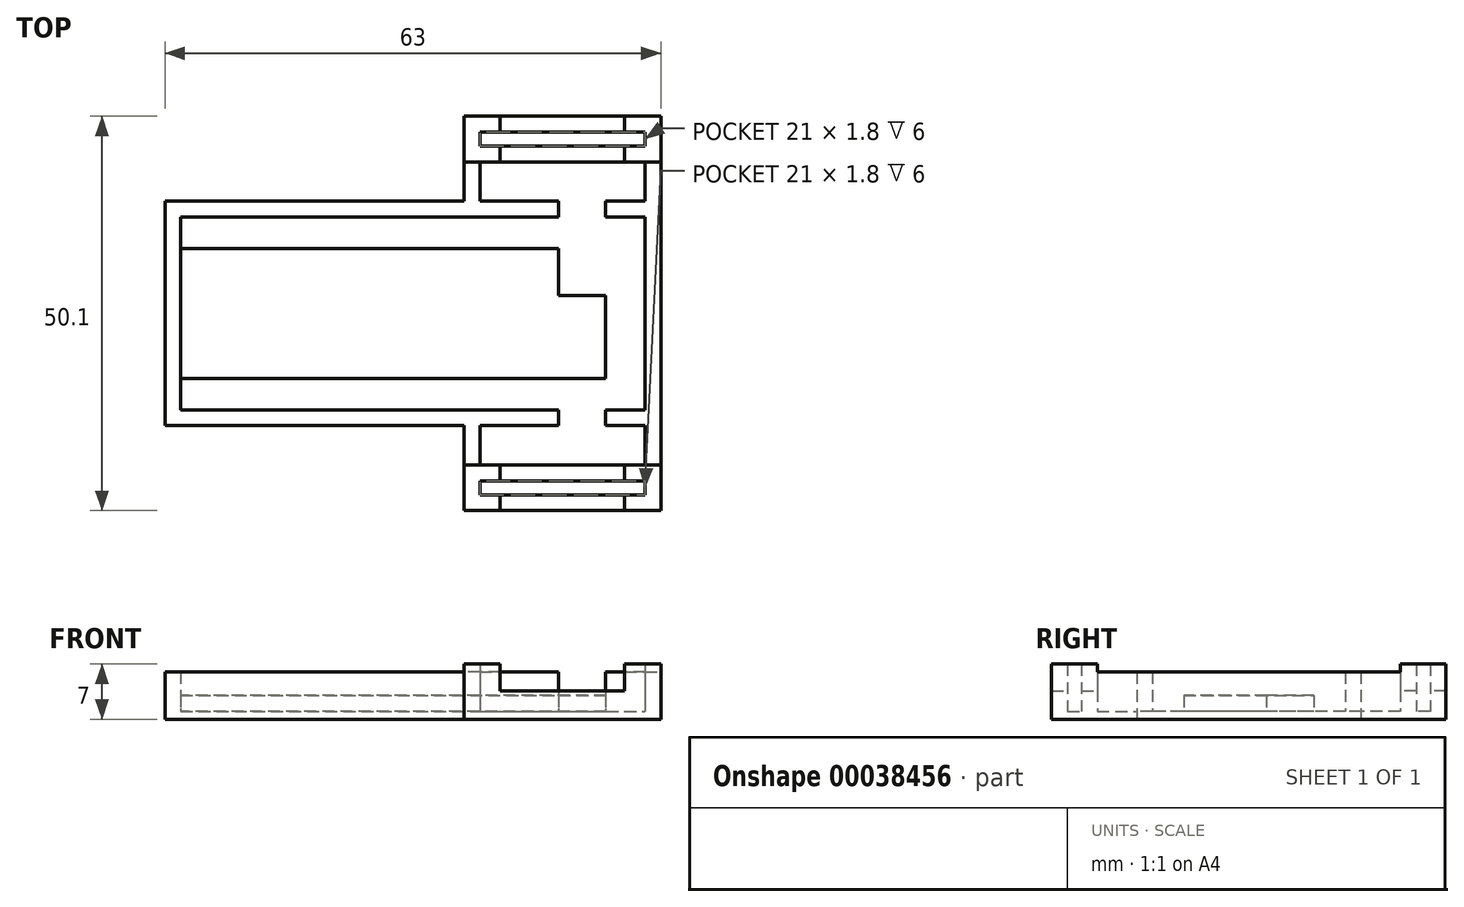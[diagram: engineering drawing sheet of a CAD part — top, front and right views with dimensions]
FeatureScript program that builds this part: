
annotation { "Feature Type Name" : "Feature", "Feature Type Description" : "" }
export const myFeature = defineFeature(function(context is Context, id is Id, definition is map)
    precondition{}
    {
        {
            var Q0;
            Q0=qCreatedBy(makeId("Top.planeOp"),FACE);
            var sketch = newSketch(context, id + "F0", { "sketchPlane" : qUnion([Q0])});
            skLineSegment(sketch, "E0", {"start": v(-83.28, 24.5) * mm, "end": v(93.04, 24.5) * mm, "construction": true});
            skLineSegment(sketch, "E1", {"start": v(59, -21.37) * mm, "end": v(59, 62.02) * mm, "construction": true});
            skLineSegment(sketch, "E2", {"start": v(-81.19, 17.1) * mm, "end": v(89.78, 17.1) * mm, "construction": true});
            skLineSegment(sketch, "E3", {"start": v(-82.58, 7.1) * mm, "end": v(88.16, 7.1) * mm, "construction": true});
            skLineSegment(sketch, "E4", {"start": v(-82.03, 20.5) * mm, "end": v(90.12, 20.5) * mm, "construction": true});
            skLineSegment(sketch, "E5", {"start": v(-82.58, 4) * mm, "end": v(90.12, 4) * mm, "construction": true});
            skLineSegment(sketch, "E6", {"start": v(54, 44.35) * mm, "end": v(54, -19.21) * mm, "construction": true});
            skLineSegment(sketch, "E7", {"start": v(-81.7, 14.5) * mm, "end": v(85.71, 14.5) * mm, "construction": true});
            skLineSegment(sketch, "E8", {"start": v(48, 44.43) * mm, "end": v(48, -19.52) * mm, "construction": true});
            skLineSegment(sketch, "E9", {"start": v(0, 20.5) * mm, "end": v(48, 20.5) * mm});
            skLineSegment(sketch, "E10", {"start": v(48, 20.5) * mm, "end": v(48, 14.5) * mm});
            skLineSegment(sketch, "E11", {"start": v(48, 14.5) * mm, "end": v(54, 14.5) * mm});
            skLineSegment(sketch, "E12", {"start": v(54, 14.5) * mm, "end": v(54, 4) * mm});
            skLineSegment(sketch, "E13", {"start": v(54, 4) * mm, "end": v(0, 4) * mm});
            skLineSegment(sketch, "E14", {"start": v(0, 4) * mm, "end": v(0, 20.5) * mm});
            skLineSegment(sketch, "E15.bottom", {"start": v(0, 24.5) * mm, "end": v(59, 24.5) * mm, "construction": true});
            skLineSegment(sketch, "E15.top", {"start": v(0, 0) * mm, "end": v(59, 0) * mm, "construction": true});
            skLineSegment(sketch, "E15.left", {"start": v(0, 24.5) * mm, "end": v(0, 0) * mm});
            skLineSegment(sketch, "E15.right", {"start": v(59, 24.5) * mm, "end": v(59, 0) * mm});
            skLineSegment(sketch, "E16.bottom", {"start": v(-2, 26.5) * mm, "end": v(61, 26.5) * mm, "construction": true});
            skLineSegment(sketch, "E16.top", {"start": v(-2, -2) * mm, "end": v(61, -2) * mm, "construction": true});
            skLineSegment(sketch, "E16.left", {"start": v(-2, 26.5) * mm, "end": v(-2, -2) * mm});
            skLineSegment(sketch, "E16.right", {"start": v(61, 26.5) * mm, "end": v(61, -2) * mm});
            skLineSegment(sketch, "E17", {"start": v(38, 55.46) * mm, "end": v(38, -21.13) * mm, "construction": true});
            skLineSegment(sketch, "E18", {"start": v(32.75, 31.5) * mm, "end": v(73.4, 31.5) * mm, "construction": true});
            skLineSegment(sketch, "E19", {"start": v(32.75, 33.5) * mm, "end": v(72.94, 33.5) * mm, "construction": true});
            skLineSegment(sketch, "E20", {"start": v(32.75, 35.3) * mm, "end": v(72.94, 35.3) * mm, "construction": true});
            skLineSegment(sketch, "E21", {"start": v(32.75, 37.3) * mm, "end": v(70.85, 37.3) * mm, "construction": true});
            skLineSegment(sketch, "E22", {"start": v(40.6, 48.4) * mm, "end": v(40.6, -32.37) * mm, "construction": true});
            skLineSegment(sketch, "E23", {"start": v(56.4, 48.1) * mm, "end": v(56.4, -31.44) * mm, "construction": true});
            skLineSegment(sketch, "E24", {"start": v(40.6, 37.3) * mm, "end": v(40.6, 35.3) * mm});
            skLineSegment(sketch, "E25", {"start": v(40.6, 35.3) * mm, "end": v(38, 35.3) * mm});
            skLineSegment(sketch, "E26", {"start": v(38, 35.3) * mm, "end": v(38, 33.5) * mm});
            skLineSegment(sketch, "E27", {"start": v(38, 33.5) * mm, "end": v(40.6, 33.5) * mm});
            skLineSegment(sketch, "E28", {"start": v(40.6, 33.5) * mm, "end": v(40.6, 31.5) * mm});
            skLineSegment(sketch, "E29", {"start": v(40.6, 31.5) * mm, "end": v(38, 31.5) * mm});
            skLineSegment(sketch, "E30", {"start": v(38, 31.5) * mm, "end": v(38, 26.5) * mm});
            skLineSegment(sketch, "E31", {"start": v(38, 26.5) * mm, "end": v(36, 26.5) * mm});
            skLineSegment(sketch, "E32", {"start": v(36, 26.5) * mm, "end": v(36, 37.3) * mm});
            skLineSegment(sketch, "E33", {"start": v(36, 37.3) * mm, "end": v(40.6, 37.3) * mm});
            skLineSegment(sketch, "E34", {"start": v(56.4, 37.3) * mm, "end": v(56.4, 35.3) * mm});
            skLineSegment(sketch, "E35", {"start": v(56.4, 35.3) * mm, "end": v(59, 35.3) * mm});
            skLineSegment(sketch, "E36", {"start": v(59, 35.3) * mm, "end": v(59, 33.5) * mm});
            skLineSegment(sketch, "E37", {"start": v(59, 33.5) * mm, "end": v(56.4, 33.5) * mm});
            skLineSegment(sketch, "E38", {"start": v(56.4, 33.5) * mm, "end": v(56.4, 31.5) * mm});
            skLineSegment(sketch, "E39", {"start": v(56.4, 31.5) * mm, "end": v(59, 31.5) * mm});
            skLineSegment(sketch, "E40", {"start": v(59, 31.5) * mm, "end": v(59, 26.5) * mm});
            skLineSegment(sketch, "E41", {"start": v(59, 26.5) * mm, "end": v(61, 26.5) * mm});
            skLineSegment(sketch, "E42", {"start": v(61, 26.5) * mm, "end": v(61, 37.3) * mm});
            skLineSegment(sketch, "E43", {"start": v(61, 37.3) * mm, "end": v(56.4, 37.3) * mm});
            skLineSegment(sketch, "E44", {"start": v(40.6, 31.5) * mm, "end": v(56.4, 31.5) * mm});
            skLineSegment(sketch, "E45", {"start": v(40.6, 33.5) * mm, "end": v(56.4, 33.5) * mm});
            skLineSegment(sketch, "E46", {"start": v(40.6, 35.3) * mm, "end": v(56.4, 35.3) * mm});
            skLineSegment(sketch, "E47", {"start": v(40.6, 37.3) * mm, "end": v(56.4, 37.3) * mm});
            skLineSegment(sketch, "E48", {"start": v(-2, 26.5) * mm, "end": v(48, 26.5) * mm});
            skLineSegment(sketch, "E49", {"start": v(48, 26.5) * mm, "end": v(48, 24.5) * mm});
            skLineSegment(sketch, "E50", {"start": v(48, 24.5) * mm, "end": v(0, 24.5) * mm});
            skLineSegment(sketch, "E51", {"start": v(61, 26.5) * mm, "end": v(54, 26.5) * mm});
            skLineSegment(sketch, "E52", {"start": v(54, 26.5) * mm, "end": v(54, 24.5) * mm});
            skLineSegment(sketch, "E53", {"start": v(54, 24.5) * mm, "end": v(59, 24.5) * mm});
            skLineSegment(sketch, "E54", {"start": v(59, 0) * mm, "end": v(54, 0) * mm});
            skLineSegment(sketch, "E55", {"start": v(54, 0) * mm, "end": v(54, -2) * mm});
            skLineSegment(sketch, "E56", {"start": v(54, -2) * mm, "end": v(61, -2) * mm});
            skLineSegment(sketch, "E57", {"start": v(0, 0) * mm, "end": v(48, 0) * mm});
            skLineSegment(sketch, "E58", {"start": v(48, 0) * mm, "end": v(48, -2) * mm});
            skLineSegment(sketch, "E59", {"start": v(48, -2) * mm, "end": v(-2, -2) * mm});
            skLineSegment(sketch, "E60", {"start": v(32.61, -7) * mm, "end": v(71.42, -7) * mm, "construction": true});
            skLineSegment(sketch, "E61", {"start": v(32.5, -9) * mm, "end": v(71.42, -9) * mm, "construction": true});
            skLineSegment(sketch, "E62", {"start": v(32.83, -10.8) * mm, "end": v(71.97, -10.8) * mm, "construction": true});
            skLineSegment(sketch, "E63", {"start": v(32.4, -12.8) * mm, "end": v(71.97, -12.8) * mm, "construction": true});
            skLineSegment(sketch, "E64", {"start": v(61, -2) * mm, "end": v(61, -12.8) * mm});
            skLineSegment(sketch, "E65", {"start": v(61, -12.8) * mm, "end": v(56.4, -12.8) * mm});
            skLineSegment(sketch, "E66", {"start": v(56.4, -12.8) * mm, "end": v(56.4, -10.8) * mm});
            skLineSegment(sketch, "E67", {"start": v(56.4, -10.8) * mm, "end": v(59, -10.8) * mm});
            skLineSegment(sketch, "E68", {"start": v(59, -10.8) * mm, "end": v(59, -9) * mm});
            skLineSegment(sketch, "E69", {"start": v(59, -9) * mm, "end": v(56.4, -9) * mm});
            skLineSegment(sketch, "E70", {"start": v(56.4, -9) * mm, "end": v(56.4, -7) * mm});
            skLineSegment(sketch, "E71", {"start": v(56.4, -7) * mm, "end": v(59, -7) * mm});
            skLineSegment(sketch, "E72", {"start": v(59, -7) * mm, "end": v(59, -2) * mm});
            skLineSegment(sketch, "E73", {"start": v(59, -2) * mm, "end": v(61, -2) * mm});
            skLineSegment(sketch, "E74", {"start": v(36, -2) * mm, "end": v(36, -12.8) * mm});
            skLineSegment(sketch, "E75", {"start": v(36, -12.8) * mm, "end": v(40.6, -12.8) * mm});
            skLineSegment(sketch, "E76", {"start": v(40.6, -12.8) * mm, "end": v(40.6, -10.8) * mm});
            skLineSegment(sketch, "E77", {"start": v(40.6, -10.8) * mm, "end": v(38, -10.8) * mm});
            skLineSegment(sketch, "E78", {"start": v(38, -10.8) * mm, "end": v(38, -9) * mm});
            skLineSegment(sketch, "E79", {"start": v(38, -9) * mm, "end": v(40.6, -9) * mm});
            skLineSegment(sketch, "E80", {"start": v(40.6, -9) * mm, "end": v(40.6, -7) * mm});
            skLineSegment(sketch, "E81", {"start": v(40.6, -7) * mm, "end": v(38, -7) * mm});
            skLineSegment(sketch, "E82", {"start": v(38, -7) * mm, "end": v(38, -2) * mm});
            skLineSegment(sketch, "E83", {"start": v(38, -2) * mm, "end": v(36, -2) * mm});
            skLineSegment(sketch, "E84", {"start": v(40.6, -12.8) * mm, "end": v(56.4, -12.8) * mm});
            skLineSegment(sketch, "E85", {"start": v(40.6, -10.8) * mm, "end": v(56.4, -10.8) * mm});
            skLineSegment(sketch, "E86", {"start": v(40.6, -9) * mm, "end": v(56.4, -9) * mm});
            skLineSegment(sketch, "E87", {"start": v(40.6, -7) * mm, "end": v(56.4, -7) * mm});
            skSolve(sketch);
        }
        {
            var Q0;
            {var subQ1=sQuery(id+"F0.wireOp",EDGE,"E9");Q0=makeQuery(id+"F0.imprint","IMPRINT",FACE,{"disambiguationData":[TD([[makeQuery(id+"F0.imprint","IMPRINT",EDGE,{"derivedFrom":subQ1}),-1.0]])]});}
            extrude(context, id + "F1", {"entities" : qUnion([Q0]), "depth" : 3 * mm});
        }
        {
            var Q0;
            {var subQ12=sQuery(id+"F0.wireOp",EDGE,"E9");Q0=makeQuery(id+"F0.imprint","IMPRINT",FACE,{"disambiguationData":[TD([[makeQuery(id+"F0.imprint","IMPRINT",EDGE,{"derivedFrom":subQ12}),1.0]])]});}
            var Q1;
            Q1=makeQuery(id+"F0.imprint","IMPRINT",FACE,{"disambiguationData":[TD([[makeQuery(id+"F0.imprint","IMPRINT",EDGE,{"derivedFrom":sQuery(id+"F0.wireOp",EDGE,"E25")}),1.0]])]});
            var Q2;
            Q2=makeQuery(id+"F0.imprint","IMPRINT",FACE,{"disambiguationData":[TD([[makeQuery(id+"F0.imprint","IMPRINT",EDGE,{"derivedFrom":sQuery(id+"F0.wireOp",EDGE,"E67")}),1.0]])]});
            extrude(context, id + "F2", {"entities" : qUnion([Q0, Q1, Q2]), "operationType" : NewBodyOperationType.ADD, "depth" : 1 * mm});
        }
        {
            var Q0;
            {var subQ10=sQuery(id+"F0.wireOp",EDGE,"E16.left");Q0=makeQuery(id+"F0.imprint","IMPRINT",FACE,{"disambiguationData":[TD([[makeQuery(id+"F0.imprint","IMPRINT",EDGE,{"derivedFrom":subQ10}),1.0]])]});}
            var Q1;
            Q1=makeQuery(id+"F0.imprint","IMPRINT",FACE,{"disambiguationData":[TD([[makeQuery(id+"F0.imprint","IMPRINT",EDGE,{"derivedFrom":sQuery(id+"F0.wireOp",EDGE,"E24")}),-1.0]])]});
            var Q2;
            Q2=makeQuery(id+"F0.imprint","IMPRINT",FACE,{"disambiguationData":[TD([[makeQuery(id+"F0.imprint","IMPRINT",EDGE,{"derivedFrom":sQuery(id+"F0.wireOp",EDGE,"E34")}),1.0]])]});
            var Q3;
            Q3=makeQuery(id+"F0.imprint","IMPRINT",FACE,{"disambiguationData":[TD([[makeQuery(id+"F0.imprint","IMPRINT",EDGE,{"derivedFrom":sQuery(id+"F0.wireOp",EDGE,"E15.right")}),1.0]])]});
            var Q4;
            Q4=makeQuery(id+"F0.imprint","IMPRINT",FACE,{"disambiguationData":[TD([[makeQuery(id+"F0.imprint","IMPRINT",EDGE,{"derivedFrom":sQuery(id+"F0.wireOp",EDGE,"E64")}),-1.0]])]});
            var Q5;
            Q5=makeQuery(id+"F0.imprint","IMPRINT",FACE,{"disambiguationData":[TD([[makeQuery(id+"F0.imprint","IMPRINT",EDGE,{"derivedFrom":sQuery(id+"F0.wireOp",EDGE,"E74")}),1.0]])]});
            extrude(context, id + "F3", {"entities" : qUnion([Q0, Q1, Q2, Q3, Q4, Q5]), "operationType" : NewBodyOperationType.ADD, "depth" : 6 * mm});
        }
        {
            var Q0;
            Q0=makeQuery(id+"F0.imprint","IMPRINT",FACE,{"disambiguationData":[TD([[makeQuery(id+"F0.imprint","IMPRINT",EDGE,{"derivedFrom":sQuery(id+"F0.wireOp",EDGE,"E24")}),1.0]])]});
            var Q1;
            Q1=makeQuery(id+"F0.imprint","IMPRINT",FACE,{"disambiguationData":[TD([[makeQuery(id+"F0.imprint","IMPRINT",EDGE,{"derivedFrom":sQuery(id+"F0.wireOp",EDGE,"E28")}),1.0]])]});
            var Q2;
            Q2=makeQuery(id+"F0.imprint","IMPRINT",FACE,{"disambiguationData":[TD([[makeQuery(id+"F0.imprint","IMPRINT",EDGE,{"derivedFrom":sQuery(id+"F0.wireOp",EDGE,"E70")}),1.0]])]});
            var Q3;
            Q3=makeQuery(id+"F0.imprint","IMPRINT",FACE,{"disambiguationData":[TD([[makeQuery(id+"F0.imprint","IMPRINT",EDGE,{"derivedFrom":sQuery(id+"F0.wireOp",EDGE,"E66")}),1.0]])]});
            extrude(context, id + "F4", {"entities" : qUnion([Q0, Q1, Q2, Q3]), "operationType" : NewBodyOperationType.ADD, "depth" : 3.6 * mm});
        }
        {
            var Q0;
            Q0=makeQuery(id+"F3.opExtrude","CAP_FACE",FACE,{"disambiguationData":[OSD([sQuery(id+"F0.wireOp",EDGE,"E15.left"),sQuery(id+"F0.wireOp",EDGE,"E16.left"),sQuery(id+"F0.wireOp",EDGE,"E24"),sQuery(id+"F0.wireOp",EDGE,"E25"),sQuery(id+"F0.wireOp",EDGE,"E26"),sQuery(id+"F0.wireOp",EDGE,"E27"),sQuery(id+"F0.wireOp",EDGE,"E28"),sQuery(id+"F0.wireOp",EDGE,"E29"),sQuery(id+"F0.wireOp",EDGE,"E30"),sQuery(id+"F0.wireOp",EDGE,"E32"),sQuery(id+"F0.wireOp",EDGE,"E33"),sQuery(id+"F0.wireOp",EDGE,"E48"),sQuery(id+"F0.wireOp",EDGE,"E49"),sQuery(id+"F0.wireOp",EDGE,"E50"),sQuery(id+"F0.wireOp",EDGE,"E57"),sQuery(id+"F0.wireOp",EDGE,"E58"),sQuery(id+"F0.wireOp",EDGE,"E59"),sQuery(id+"F0.wireOp",EDGE,"E74"),sQuery(id+"F0.wireOp",EDGE,"E75"),sQuery(id+"F0.wireOp",EDGE,"E76"),sQuery(id+"F0.wireOp",EDGE,"E77"),sQuery(id+"F0.wireOp",EDGE,"E78"),sQuery(id+"F0.wireOp",EDGE,"E79"),sQuery(id+"F0.wireOp",EDGE,"E80"),sQuery(id+"F0.wireOp",EDGE,"E81"),sQuery(id+"F0.wireOp",EDGE,"E82")])],"isStart":false});
            var sketch = newSketch(context, id + "F5", { "sketchPlane" : qUnion([Q0])});
            skLineSegment(sketch, "E88", {"start": v(36, 37.3) * mm, "end": v(40.6, 37.3) * mm});
            skLineSegment(sketch, "E89", {"start": v(40.6, 37.3) * mm, "end": v(40.6, 35.3) * mm});
            skLineSegment(sketch, "E90", {"start": v(40.6, 35.3) * mm, "end": v(38, 35.3) * mm});
            skLineSegment(sketch, "E91", {"start": v(38, 35.3) * mm, "end": v(38, 33.5) * mm});
            skLineSegment(sketch, "E92", {"start": v(38, 33.5) * mm, "end": v(40.6, 33.5) * mm});
            skLineSegment(sketch, "E93", {"start": v(40.6, 33.5) * mm, "end": v(40.6, 31.5) * mm});
            skLineSegment(sketch, "E94", {"start": v(40.6, 31.5) * mm, "end": v(36, 31.5) * mm});
            skPoint(sketch, "E94.endSnap0", {"position": v(39.3, 31.5) * mm});
            skLineSegment(sketch, "E95", {"start": v(36, 31.5) * mm, "end": v(36, 37.3) * mm});
            skLineSegment(sketch, "E96", {"start": v(40.6, -7) * mm, "end": v(36, -7) * mm});
            skLineSegment(sketch, "E97", {"start": v(36, -7) * mm, "end": v(36, -12.8) * mm});
            skLineSegment(sketch, "E98", {"start": v(36, -12.8) * mm, "end": v(40.6, -12.8) * mm});
            skLineSegment(sketch, "E99", {"start": v(40.6, -12.8) * mm, "end": v(40.6, -10.8) * mm});
            skLineSegment(sketch, "E100", {"start": v(40.6, -10.8) * mm, "end": v(38, -10.8) * mm});
            skLineSegment(sketch, "E101", {"start": v(38, -10.8) * mm, "end": v(38, -9) * mm});
            skLineSegment(sketch, "E102", {"start": v(38, -9) * mm, "end": v(40.6, -9) * mm});
            skLineSegment(sketch, "E103", {"start": v(40.6, -9) * mm, "end": v(40.6, -7) * mm});
            skSolve(sketch);
        }
        {
            var Q0;
            Q0=makeQuery(id+"F3.opExtrude","CAP_FACE",FACE,{"disambiguationData":[OSD([sQuery(id+"F0.wireOp",EDGE,"E15.right"),sQuery(id+"F0.wireOp",EDGE,"E16.right"),sQuery(id+"F0.wireOp",EDGE,"E34"),sQuery(id+"F0.wireOp",EDGE,"E35"),sQuery(id+"F0.wireOp",EDGE,"E36"),sQuery(id+"F0.wireOp",EDGE,"E37"),sQuery(id+"F0.wireOp",EDGE,"E38"),sQuery(id+"F0.wireOp",EDGE,"E39"),sQuery(id+"F0.wireOp",EDGE,"E40"),sQuery(id+"F0.wireOp",EDGE,"E42"),sQuery(id+"F0.wireOp",EDGE,"E43"),sQuery(id+"F0.wireOp",EDGE,"E51"),sQuery(id+"F0.wireOp",EDGE,"E52"),sQuery(id+"F0.wireOp",EDGE,"E53"),sQuery(id+"F0.wireOp",EDGE,"E54"),sQuery(id+"F0.wireOp",EDGE,"E55"),sQuery(id+"F0.wireOp",EDGE,"E56"),sQuery(id+"F0.wireOp",EDGE,"E64"),sQuery(id+"F0.wireOp",EDGE,"E65"),sQuery(id+"F0.wireOp",EDGE,"E66"),sQuery(id+"F0.wireOp",EDGE,"E67"),sQuery(id+"F0.wireOp",EDGE,"E68"),sQuery(id+"F0.wireOp",EDGE,"E69"),sQuery(id+"F0.wireOp",EDGE,"E70"),sQuery(id+"F0.wireOp",EDGE,"E71"),sQuery(id+"F0.wireOp",EDGE,"E72")])],"isStart":false});
            var sketch = newSketch(context, id + "F6", { "sketchPlane" : qUnion([Q0])});
            skLineSegment(sketch, "E104", {"start": v(56.4, 37.3) * mm, "end": v(56.4, 35.3) * mm});
            skLineSegment(sketch, "E105", {"start": v(56.4, 35.3) * mm, "end": v(59, 35.3) * mm});
            skLineSegment(sketch, "E106", {"start": v(59, 35.3) * mm, "end": v(59, 33.5) * mm});
            skLineSegment(sketch, "E107", {"start": v(59, 33.5) * mm, "end": v(56.4, 33.5) * mm});
            skLineSegment(sketch, "E108", {"start": v(56.4, 33.5) * mm, "end": v(56.4, 31.5) * mm});
            skLineSegment(sketch, "E109", {"start": v(56.4, 31.5) * mm, "end": v(61, 31.5) * mm});
            skLineSegment(sketch, "E110", {"start": v(61, 31.5) * mm, "end": v(61, 37.3) * mm});
            skLineSegment(sketch, "E111", {"start": v(61, 37.3) * mm, "end": v(56.4, 37.3) * mm});
            skLineSegment(sketch, "E112", {"start": v(56.4, -7) * mm, "end": v(61, -7) * mm});
            skLineSegment(sketch, "E113", {"start": v(61, -7) * mm, "end": v(61, -12.8) * mm});
            skLineSegment(sketch, "E114", {"start": v(61, -12.8) * mm, "end": v(56.4, -12.8) * mm});
            skLineSegment(sketch, "E115", {"start": v(56.4, -12.8) * mm, "end": v(56.4, -10.8) * mm});
            skLineSegment(sketch, "E116", {"start": v(56.4, -10.8) * mm, "end": v(59, -10.8) * mm});
            skLineSegment(sketch, "E117", {"start": v(59, -10.8) * mm, "end": v(59, -9) * mm});
            skLineSegment(sketch, "E118", {"start": v(59, -9) * mm, "end": v(56.4, -9) * mm});
            skLineSegment(sketch, "E119", {"start": v(56.4, -9) * mm, "end": v(56.4, -7) * mm});
            skSolve(sketch);
        }
        {
            var Q0;
            Q0 = qSketchRegion(id + "F6", true);
            var Q1;
            Q1=makeQuery(id+"F5.imprint","IMPRINT",FACE,{"disambiguationData":[TD([[makeQuery(id+"F5.imprint","IMPRINT",EDGE,{"derivedFrom":sQuery(id+"F5.wireOp",EDGE,"E88")}),-1.0]])]});
            var Q2;
            {var subQ0=sQuery(id+"F5.wireOp",EDGE,"E97");Q2=makeQuery(id+"F5.imprint","IMPRINT",FACE,{"disambiguationData":[TD([[makeQuery(id+"F5.imprint","IMPRINT",EDGE,{"derivedFrom":subQ0}),1.0]])]});}
            extrude(context, id + "F7", {"entities" : qUnion([Q0, Q1, Q2]), "operationType" : NewBodyOperationType.ADD, "depth" : 1 * mm});
        }
    });
